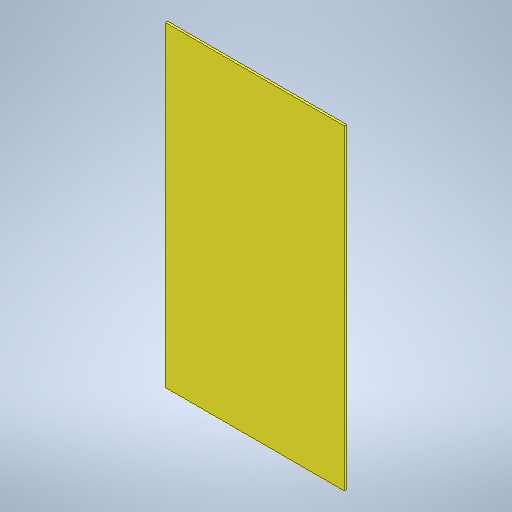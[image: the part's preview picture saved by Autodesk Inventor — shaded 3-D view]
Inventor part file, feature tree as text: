
AUTODESK INVENTOR PART (.ipt)
format: ipt  version: 2025 (Build 290162010, 162A)  size: 244,224 bytes
history: native  units: in
note: dims shown in document units (in); Inventor stores cm internally (conversion verified against a paired STEP export)
features: extrude x1, sketch x1
ambient origin geometry x8: Origin, YZ Plane, XZ Plane, XY Plane, X Axis, Y Axis, Z Axis, Center Point
bodies: Solid1 (feature_tree)
feature tree (2):
  extrude  "Extrusion1"  Depth=48.0in
  sketch  "Sketch1"  dims[d2=84.5in d3=48.0in d4=0.625in d5=0.0in]
